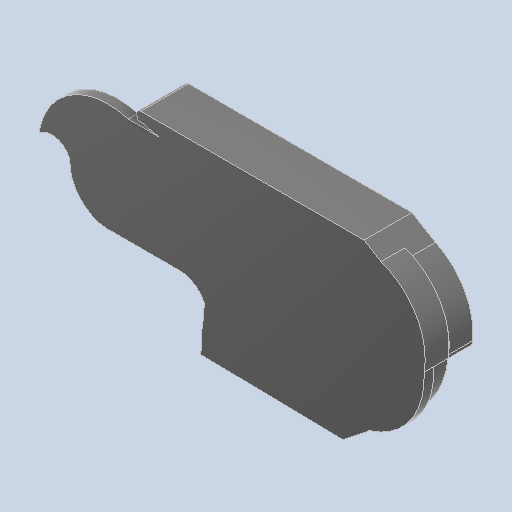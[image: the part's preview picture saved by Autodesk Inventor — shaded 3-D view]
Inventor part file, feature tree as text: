
AUTODESK INVENTOR PART (.ipt)
format: ipt  version: 2022 (Build 260153000, 153)  size: 423,936 bytes
history: native  units: in
note: dims shown in document units (in); Inventor stores cm internally (conversion verified against a paired STEP export)
features: extrude x6, sketch x6, other x1
ambient origin geometry x8: Origin, YZ Plane, XZ Plane, XY Plane, X Axis, Y Axis, Z Axis, Center Point
bodies: Body1 (feature_tree)
feature tree (13):
  other  "Sólido1"
  extrude  "Extrusión1"  Depth=0.0709in TaperAngle=0.0deg
  extrude  "Extrusión2"  Depth=0.0472in TaperAngle=0.0deg
  extrude  "Extrusión3"  Depth=0.0787in
  extrude  "Extrusión4"  Depth=0.1181in TaperAngle=0.0deg
  extrude  "Extrusión5"  Depth=0.0197in
  extrude  "Extrusión8"  Depth=0.0197in
  sketch  "Boceto1"  dims[d5=0.0472in d6=0.0in d7=0.0709in d8=0.0in]
  sketch  "Boceto2"  dims[d9=0.2362in d10=0.0in d11=0.0472in d12=0.0in]
  sketch  "Boceto3"  dims[d13=0.0472in d14=0.0in d15=0.0787in]
  sketch  "Boceto4"  dims[d16=0.0197in d23=0.1181in d24=0.0in]
  sketch  "Boceto5"  dims[d25=0.0197in d26=0.0344in]
  sketch  "Boceto13"  dims[d27=0.0197in d28=0.0344in]
